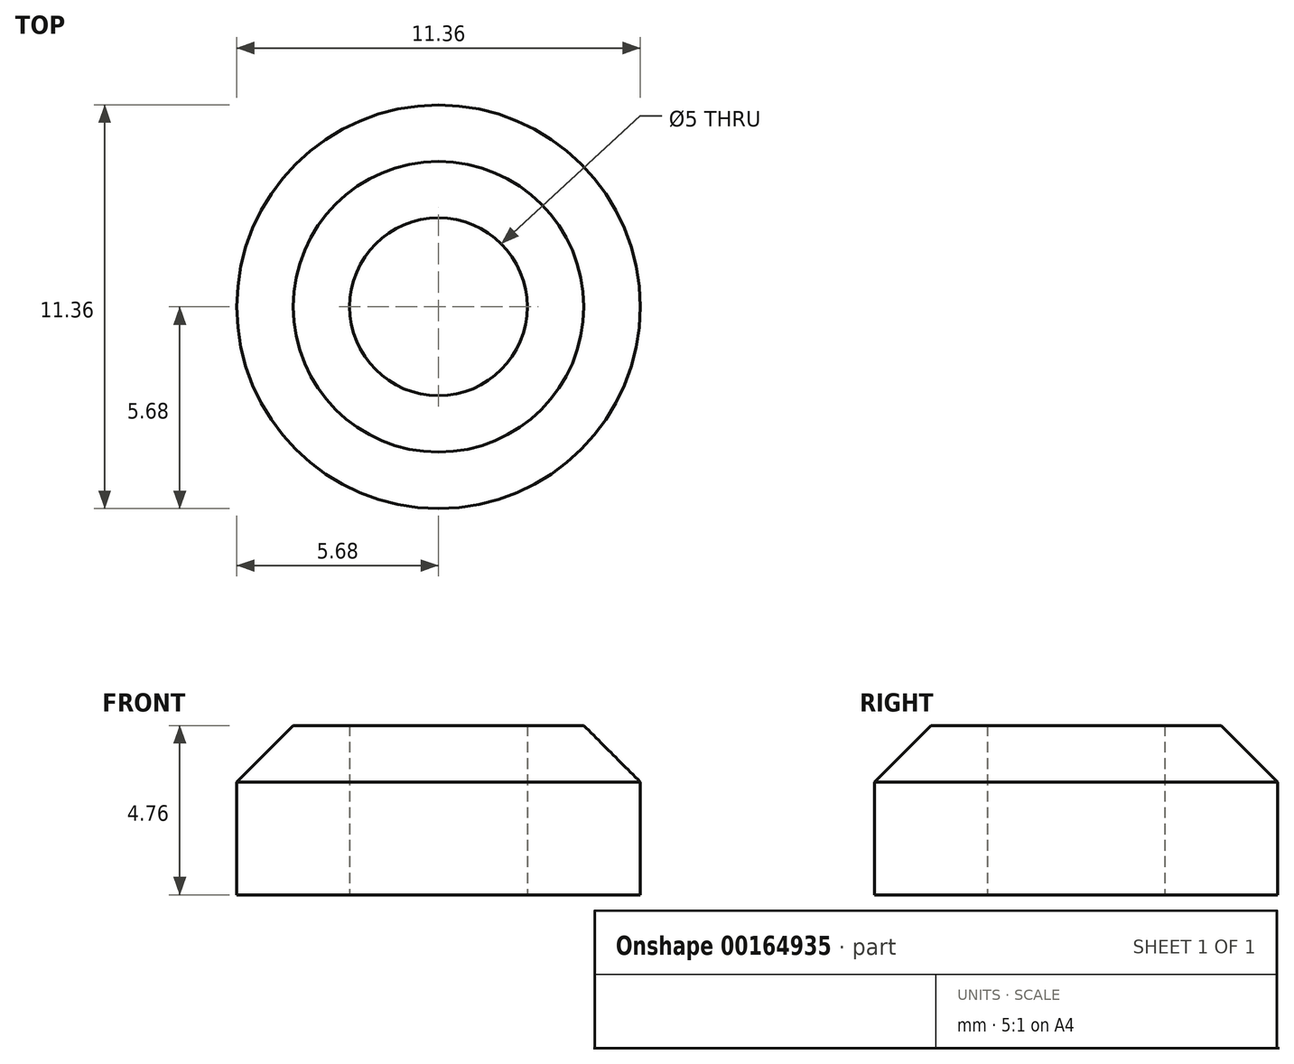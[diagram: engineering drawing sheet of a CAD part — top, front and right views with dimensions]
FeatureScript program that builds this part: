
annotation { "Feature Type Name" : "Feature", "Feature Type Description" : "" }
export const myFeature = defineFeature(function(context is Context, id is Id, definition is map)
    precondition{}
    {
        {
            var Q0;
            Q0=qCreatedBy(makeId("Top.planeOp"),FACE);
            var sketch = newSketch(context, id + "F0", { "sketchPlane" : qUnion([Q0])});
            skCircle(sketch, "E0", {"center": v(0, 0) * mm, "radius": 2.5 * mm});
            skCircle(sketch, "E1", {"center": v(0, 0) * mm, "radius": 5.68 * mm});
            skSolve(sketch);
        }
        {
            var Q0;
            Q0=qSketchRegion(id+"F0",true);
            extrude(context, id + "F1", {"entities" : qUnion([Q0]), "depth" : 4.76 * mm});
        }
        {
            var Q0;
            Q0=makeQuery(id+"F1.opExtrude","CAP_EDGE",EDGE,{"disambiguationData":[OSD([sQuery(id+"F0.wireOp",EDGE,"E1")])],"isStart":false});
            chamfer(context, id + "F2", {"entities" : qUnion([Q0]), "width" : 1.59 * mm, "tangentPropagation" : true});
        }
    });
